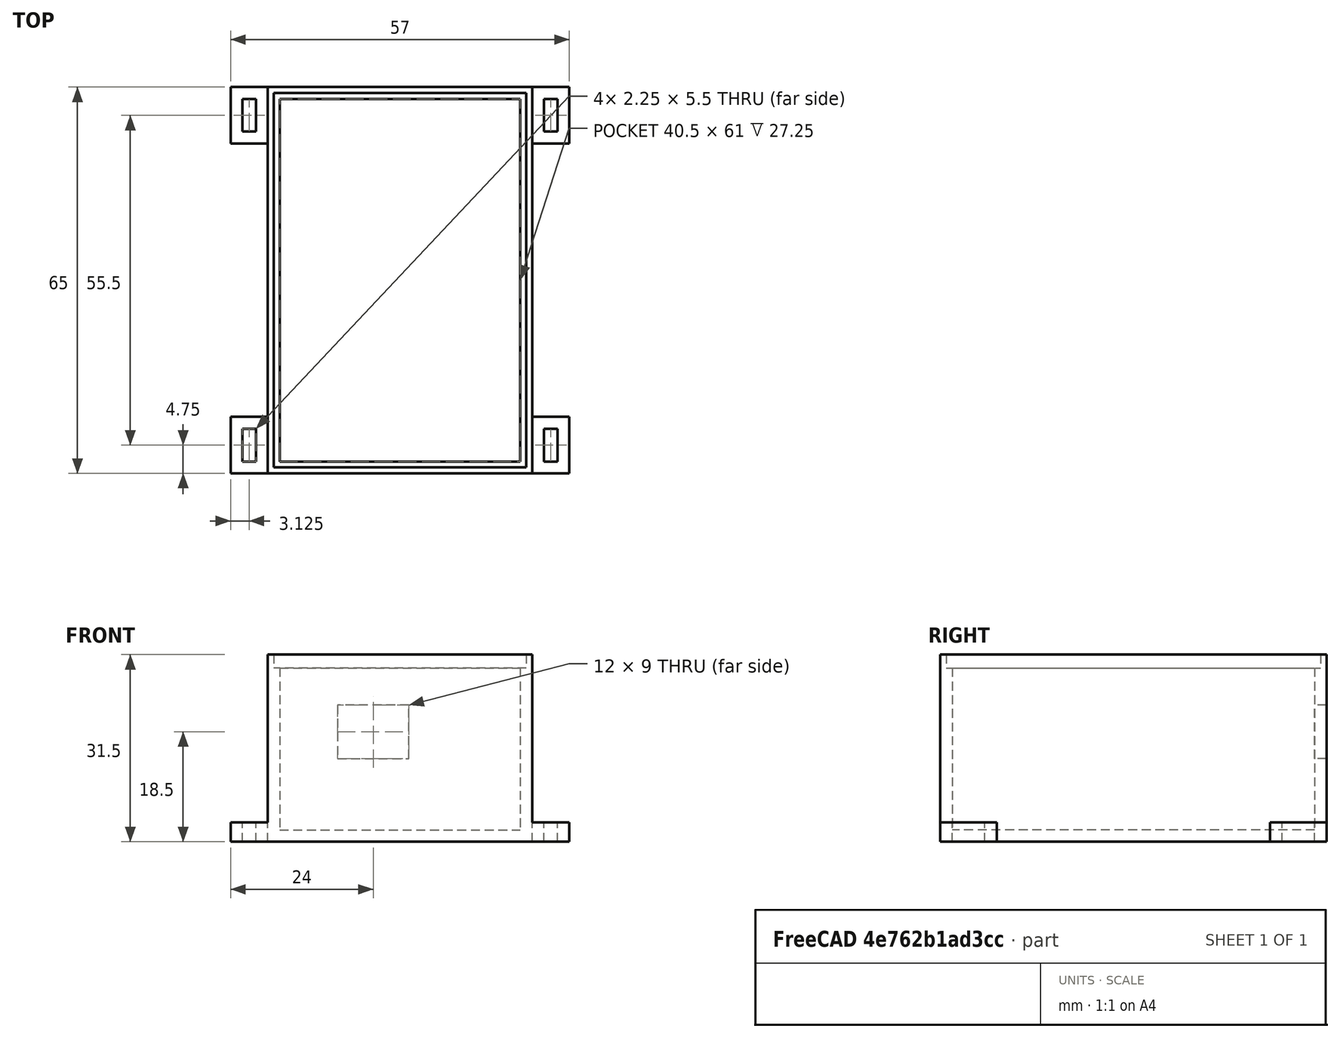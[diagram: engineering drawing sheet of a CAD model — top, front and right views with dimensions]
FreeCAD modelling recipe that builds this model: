
FCSTD DOCUMENT  (FreeCAD 0.19R)
Label: control-board-mount-base
License: All rights reserved
LicenseURL: http://en.wikipedia.org/wiki/All_rights_reserved
objects: Sketcher::SketchObject×5, PartDesign::Pocket×3, PartDesign::Pad×2, PartDesign::Body×1, Mesh::Feature×1
note: 16 computed .brp shape members not serialized (recipe doc carries the construction recipe); baked Part::Feature solids carry a one-line shape summary decoded from their .brp

FEATURE [Sketcher::SketchObject] Sketch
  FullyConstrained = true
  MapMode = 5
  Support = -> [XY_Plane]
  sketch-geometry (4):
    g0: LineSegment StartX=0 StartY=0 StartZ=0 EndX=44.5 EndY=0 EndZ=0
    g1: LineSegment StartX=44.5 StartY=0 StartZ=0 EndX=44.5 EndY=65 EndZ=0
    g2: LineSegment StartX=44.5 StartY=65 StartZ=0 EndX=0 EndY=65 EndZ=0
    g3: LineSegment StartX=0 StartY=65 StartZ=0 EndX=0 EndY=0 EndZ=0
  constraints (11):
    c: Coincident(g0,g1)
    c: Coincident(g1,g2)
    c: Coincident(g2,g3)
    c: Coincident(g3,g0)
    c: Horizontal(g0)
    c: Horizontal(g2)
    c: Vertical(g1)
    c: Vertical(g3)
    c: Coincident(g0,g-1)
    c: DistanceX(g2,g2) = 44.5
    c: DistanceY(g1,g1) = 65
FEATURE [PartDesign::Pad] Pad
  Direction = (1,1,1)
  Length = 31.5
  Length2 = 100
  Profile = -> Sketch
  Type = 0
FEATURE [Sketcher::SketchObject] Sketch001
  FullyConstrained = true
  MapMode = 5
  Placement = pos=(0,0,31.5) rot=(0,0,1;0rad)
  Support = -> [Pad]
  sketch-geometry (10):
    g0: LineSegment StartX=1 StartY=64 StartZ=0 EndX=43.5 EndY=64 EndZ=0
    g1: LineSegment StartX=43.5 StartY=64 StartZ=0 EndX=43.5 EndY=1 EndZ=0
    g2: LineSegment StartX=43.5 StartY=1 StartZ=0 EndX=1 EndY=1 EndZ=0
    g3: LineSegment StartX=1 StartY=1 StartZ=0 EndX=1 EndY=64 EndZ=0
    g4: LineSegment StartX=0 StartY=0 StartZ=0 EndX=44.5 EndY=0 EndZ=0
    g5: LineSegment StartX=44.5 StartY=0 StartZ=0 EndX=44.5 EndY=65 EndZ=0
    g6: LineSegment StartX=44.5 StartY=65 StartZ=0 EndX=0 EndY=65 EndZ=0
    g7: LineSegment StartX=0 StartY=65 StartZ=0 EndX=0 EndY=0 EndZ=0
    g8: LineSegment StartX=22.25 StartY=64 StartZ=0 EndX=22.25 EndY=65 EndZ=0
    g9: LineSegment StartX=43.5 StartY=32.5 StartZ=0 EndX=44.5 EndY=32.5 EndZ=0
  constraints (27):
    c: Coincident(g0,g1)
    c: Coincident(g1,g2)
    c: Coincident(g2,g3)
    c: Coincident(g3,g0)
    c: Horizontal(g0)
    c: Horizontal(g2)
    c: Vertical(g1)
    c: Vertical(g3)
    c: Coincident(g4,g5)
    c: Coincident(g5,g6)
    c: Coincident(g6,g7)
    c: Coincident(g7,g4)
    c: Horizontal(g4)
    c: Horizontal(g6)
    c: Vertical(g5)
    c: Vertical(g7)
    c: Coincident(g4,g-1)
    c: DistanceX(g6,g6) = 44.5
    c: DistanceY(g5,g5) = 65
    c: Vertical(g8)
    c: Horizontal(g9)
    c: Symmetric(g5,g6,g8)
    c: Symmetric(g0,g0,g8)
    c: Symmetric(g4,g5,g9)
    c: Symmetric(g1,g0,g9)
    c: DistanceX(g6,g0) = 1
    c: DistanceY(g0,g6) = 1
FEATURE [PartDesign::Pocket] Pocket
  BaseFeature = -> Pad
  Length = 2.25
  Length2 = 100
  Profile = -> Sketch001
  Type = 0
FEATURE [Sketcher::SketchObject] Sketch002
  FullyConstrained = true
  MapMode = 5
  Placement = pos=(0,0,29.25) rot=(0,0,1;0rad)
  Support = -> [Pocket]
  sketch-geometry (10):
    g0: LineSegment StartX=2 StartY=63 StartZ=0 EndX=42.5 EndY=63 EndZ=0
    g1: LineSegment StartX=42.5 StartY=63 StartZ=0 EndX=42.5 EndY=2 EndZ=0
    g2: LineSegment StartX=42.5 StartY=2 StartZ=0 EndX=2 EndY=2 EndZ=0
    g3: LineSegment StartX=2 StartY=2 StartZ=0 EndX=2 EndY=63 EndZ=0
    g4: LineSegment StartX=0 StartY=0 StartZ=0 EndX=44.5 EndY=0 EndZ=0
    g5: LineSegment StartX=44.5 StartY=0 StartZ=0 EndX=44.5 EndY=65 EndZ=0
    g6: LineSegment StartX=44.5 StartY=65 StartZ=0 EndX=0 EndY=65 EndZ=0
    g7: LineSegment StartX=0 StartY=65 StartZ=0 EndX=0 EndY=0 EndZ=0
    g8: LineSegment StartX=22.25 StartY=63 StartZ=0 EndX=22.25 EndY=65 EndZ=0
    g9: LineSegment StartX=42.5 StartY=32.5 StartZ=0 EndX=44.5 EndY=32.5 EndZ=0
  constraints (27):
    c: Coincident(g0,g1)
    c: Coincident(g1,g2)
    c: Coincident(g2,g3)
    c: Coincident(g3,g0)
    c: Horizontal(g0)
    c: Horizontal(g2)
    c: Vertical(g1)
    c: Vertical(g3)
    c: Coincident(g4,g5)
    c: Coincident(g5,g6)
    c: Coincident(g6,g7)
    c: Coincident(g7,g4)
    c: Horizontal(g4)
    c: Horizontal(g6)
    c: Vertical(g5)
    c: Vertical(g7)
    c: Coincident(g4,g-1)
    c: Vertical(g8)
    c: Horizontal(g9)
    c: Symmetric(g5,g6,g8)
    c: Symmetric(g0,g0,g8)
    c: Symmetric(g4,g5,g9)
    c: Symmetric(g1,g0,g9)
    c: DistanceX(g6,g6) = 44.5
    c: DistanceY(g5,g5) = 65
    c: DistanceX(g6,g0) = 2
    c: DistanceY(g0,g6) = 2
FEATURE [PartDesign::Pocket] Pocket001
  BaseFeature = -> Pocket
  Length = 27.25
  Length2 = 100
  Profile = -> Sketch002
  Type = 0
FEATURE [Sketcher::SketchObject] Sketch003
  FullyConstrained = true
  MapMode = 5
  Placement = pos=(0,65,0) rot=(0,0.707107,0.707107;3.14159rad)
  Support = -> [Pocket001]
  sketch-geometry (15):
    g0: LineSegment StartX=-23.75 StartY=23 StartZ=0 EndX=-11.75 EndY=23 EndZ=0
    g1: LineSegment StartX=-11.75 StartY=23 StartZ=0 EndX=-11.75 EndY=14 EndZ=0
    g2: LineSegment StartX=-11.75 StartY=14 StartZ=0 EndX=-23.75 EndY=14 EndZ=0
    g3: LineSegment StartX=-23.75 StartY=14 StartZ=0 EndX=-23.75 EndY=23 EndZ=0
    g4: LineSegment StartX=-2.25 StartY=2 StartZ=0 EndX=-42.25 EndY=2 EndZ=0
    g5: LineSegment StartX=-42.25 StartY=2 StartZ=0 EndX=-42.25 EndY=29 EndZ=0
    g6: LineSegment StartX=-42.25 StartY=29 StartZ=0 EndX=-2.25 EndY=29 EndZ=0
    g7: LineSegment StartX=-2.25 StartY=29 StartZ=0 EndX=-2.25 EndY=2 EndZ=0
    g8: GeomPoint X=-17.75 Y=14 Z=0
    g9: GeomPoint X=-11.75 Y=18.5 Z=0
    g10: LineSegment StartX=-44.5 StartY=31.5 StartZ=0 EndX=0 EndY=31.5 EndZ=0
    g11: LineSegment StartX=0 StartY=31.5 StartZ=0 EndX=0 EndY=0 EndZ=0
    g12: LineSegment StartX=0 StartY=0 StartZ=0 EndX=-44.5 EndY=0 EndZ=0
    g13: LineSegment StartX=-44.5 StartY=0 StartZ=0 EndX=-44.5 EndY=31.5 EndZ=0
    g14: LineSegment StartX=-22.25 StartY=29 StartZ=0 EndX=-22.25 EndY=31.5 EndZ=0
  constraints (39):
    c: Coincident(g0,g1)
    c: Coincident(g1,g2)
    c: Coincident(g2,g3)
    c: Coincident(g3,g0)
    c: Horizontal(g0)
    c: Horizontal(g2)
    c: Vertical(g1)
    c: Vertical(g3)
    c: Coincident(g4,g5)
    c: Coincident(g5,g6)
    c: Coincident(g6,g7)
    c: Coincident(g7,g4)
    c: Horizontal(g4)
    c: Horizontal(g6)
    c: Vertical(g5)
    c: Vertical(g7)
    c: DistanceX(g4,g4) = 40
    c: DistanceY(g7,g7) = 27
    c: DistanceX(g0,g0) = 12
    c: DistanceY(g3,g3) = 9
    c: Symmetric(g1,g0,g9)
    c: Symmetric(g1,g2,g8)
    c: DistanceX(g8,g4) = 15.5
    c: Coincident(g10,g11)
    c: Coincident(g11,g12)
    c: Coincident(g12,g13)
    c: Coincident(g13,g10)
    c: Horizontal(g10)
    c: Horizontal(g12)
    c: Vertical(g11)
    c: Vertical(g13)
    c: Coincident(g11,g-1)
    c: DistanceX(g10,g10) = 44.5
    c: Vertical(g14)
    c: Symmetric(g6,g5,g14)
    c: Symmetric(g10,g10,g14)
    c: DistanceY(g13,g13) = 31.5
    c: DistanceY(g12,g4) = 2
    c: DistanceY(g9,g6) = 10.5
FEATURE [PartDesign::Pocket] Pocket002
  BaseFeature = -> Pocket001
  Length = 5
  Length2 = 100
  Profile = -> Sketch003
  Type = 2
FEATURE [Sketcher::SketchObject] Sketch004
  FullyConstrained = true
  MapMode = 5
  Support = -> [XY_Plane]
  sketch-geometry (44):
    g0: LineSegment StartX=0 StartY=0 StartZ=0 EndX=44.5 EndY=0 EndZ=0
    g1: LineSegment StartX=44.5 StartY=0 StartZ=0 EndX=44.5 EndY=65 EndZ=0
    g2: LineSegment StartX=44.5 StartY=65 StartZ=0 EndX=0 EndY=65 EndZ=0
    g3: LineSegment StartX=0 StartY=65 StartZ=0 EndX=0 EndY=0 EndZ=0
    g4: LineSegment StartX=44.5 StartY=65 StartZ=0 EndX=50.75 EndY=65 EndZ=0
    g5: LineSegment StartX=50.75 StartY=65 StartZ=0 EndX=50.75 EndY=55.5 EndZ=0
    g6: LineSegment StartX=50.75 StartY=55.5 StartZ=0 EndX=44.5 EndY=55.5 EndZ=0
    g7: LineSegment StartX=44.5 StartY=55.5 StartZ=0 EndX=44.5 EndY=65 EndZ=0
    g8: LineSegment StartX=44.5 StartY=0 StartZ=0 EndX=50.75 EndY=0 EndZ=0
    g9: LineSegment StartX=50.75 StartY=0 StartZ=0 EndX=50.75 EndY=9.5 EndZ=0
    g10: LineSegment StartX=50.75 StartY=9.5 StartZ=0 EndX=44.5 EndY=9.5 EndZ=0
    g11: LineSegment StartX=44.5 StartY=9.5 StartZ=0 EndX=44.5 EndY=0 EndZ=0
    g12: LineSegment StartX=0 StartY=0 StartZ=0 EndX=-6.25 EndY=0 EndZ=0
    g13: LineSegment StartX=-6.25 StartY=0 StartZ=0 EndX=-6.25 EndY=9.5 EndZ=0
    g14: LineSegment StartX=-6.25 StartY=9.5 StartZ=0 EndX=0 EndY=9.5 EndZ=0
    g15: LineSegment StartX=0 StartY=9.5 StartZ=0 EndX=0 EndY=0 EndZ=0
    g16: LineSegment StartX=0 StartY=65 StartZ=0 EndX=-6.25 EndY=65 EndZ=0
    g17: LineSegment StartX=-6.25 StartY=65 StartZ=0 EndX=-6.25 EndY=55.5 EndZ=0
    g18: LineSegment StartX=-6.25 StartY=55.5 StartZ=0 EndX=0 EndY=55.5 EndZ=0
    g19: LineSegment StartX=0 StartY=55.5 StartZ=0 EndX=0 EndY=65 EndZ=0
    g20: LineSegment StartX=46.5 StartY=63 StartZ=0 EndX=48.75 EndY=63 EndZ=0
    g21: LineSegment StartX=48.75 StartY=63 StartZ=0 EndX=48.75 EndY=57.5 EndZ=0
    g22: LineSegment StartX=48.75 StartY=57.5 StartZ=0 EndX=46.5 EndY=57.5 EndZ=0
    g23: LineSegment StartX=46.5 StartY=57.5 StartZ=0 EndX=46.5 EndY=63 EndZ=0
    g24: LineSegment StartX=46.5 StartY=7.5 StartZ=0 EndX=48.75 EndY=7.5 EndZ=0
    g25: LineSegment StartX=48.75 StartY=7.5 StartZ=0 EndX=48.75 EndY=2 EndZ=0
    g26: LineSegment StartX=48.75 StartY=2 StartZ=0 EndX=46.5 EndY=2 EndZ=0
    g27: LineSegment StartX=46.5 StartY=2 StartZ=0 EndX=46.5 EndY=7.5 EndZ=0
    g28: LineSegment StartX=-4.25 StartY=7.5 StartZ=0 EndX=-2 EndY=7.5 EndZ=0
    g29: LineSegment StartX=-2 StartY=7.5 StartZ=0 EndX=-2 EndY=2 EndZ=0
    g30: LineSegment StartX=-2 StartY=2 StartZ=0 EndX=-4.25 EndY=2 EndZ=0
    g31: LineSegment StartX=-4.25 StartY=2 StartZ=0 EndX=-4.25 EndY=7.5 EndZ=0
    g32: LineSegment StartX=-4.25 StartY=63 StartZ=0 EndX=-2 EndY=63 EndZ=0
    g33: LineSegment StartX=-2 StartY=63 StartZ=0 EndX=-2 EndY=57.5 EndZ=0
    g34: LineSegment StartX=-2 StartY=57.5 StartZ=0 EndX=-4.25 EndY=57.5 EndZ=0
    g35: LineSegment StartX=-4.25 StartY=57.5 StartZ=0 EndX=-4.25 EndY=63 EndZ=0
    g36: LineSegment StartX=-3.125 StartY=63 StartZ=0 EndX=-3.125 EndY=65 EndZ=0
    g37: LineSegment StartX=-4.25 StartY=60.25 StartZ=0 EndX=-6.25 EndY=60.25 EndZ=0
    g38: LineSegment StartX=47.625 StartY=63 StartZ=0 EndX=47.625 EndY=65 EndZ=0
    g39: LineSegment StartX=48.75 StartY=60.25 StartZ=0 EndX=50.75 EndY=60.25 EndZ=0
    g40: LineSegment StartX=-3.125 StartY=7.5 StartZ=0 EndX=-3.125 EndY=9.5 EndZ=0
    g41: LineSegment StartX=-4.25 StartY=4.75 StartZ=0 EndX=-6.25 EndY=4.75 EndZ=0
    g42: LineSegment StartX=47.625 StartY=7.5 StartZ=0 EndX=47.625 EndY=9.5 EndZ=0
    g43: LineSegment StartX=48.75 StartY=4.75 StartZ=0 EndX=50.75 EndY=4.75 EndZ=0
  constraints (119):
    c: Coincident(g0,g1)
    c: Coincident(g1,g2)
    c: Coincident(g2,g3)
    c: Coincident(g3,g0)
    c: Horizontal(g0)
    c: Horizontal(g2)
    c: Vertical(g1)
    c: Vertical(g3)
    c: Coincident(g0,g-1)
    c: Coincident(g4,g5)
    c: Coincident(g5,g6)
    c: Coincident(g6,g7)
    c: Coincident(g7,g4)
    c: Horizontal(g4)
    c: Horizontal(g6)
    c: Vertical(g5)
    c: Vertical(g7)
    c: Coincident(g4,g1)
    c: Coincident(g8,g9)
    c: Coincident(g9,g10)
    c: Coincident(g10,g11)
    c: Coincident(g11,g8)
    c: Horizontal(g8)
    c: Horizontal(g10)
    c: Vertical(g9)
    c: Vertical(g11)
    c: Coincident(g8,g0)
    c: Coincident(g12,g13)
    c: Coincident(g13,g14)
    c: Coincident(g14,g15)
    c: Coincident(g15,g12)
    c: Horizontal(g12)
    c: Horizontal(g14)
    c: Vertical(g13)
    c: Vertical(g15)
    c: Coincident(g12,g-1)
    c: Coincident(g16,g17)
    c: Coincident(g17,g18)
    c: Coincident(g18,g19)
    c: Coincident(g19,g16)
    c: Horizontal(g16)
    c: Horizontal(g18)
    c: Vertical(g17)
    c: Vertical(g19)
    c: Coincident(g16,g2)
    c: Coincident(g20,g21)
    c: Coincident(g21,g22)
    c: Coincident(g22,g23)
    c: Coincident(g23,g20)
    c: Horizontal(g20)
    c: Horizontal(g22)
    c: Vertical(g21)
    c: Vertical(g23)
    c: Coincident(g24,g25)
    c: Coincident(g25,g26)
    c: Coincident(g26,g27)
    c: Coincident(g27,g24)
    c: Horizontal(g24)
    c: Horizontal(g26)
    c: Vertical(g25)
    c: Vertical(g27)
    c: Coincident(g28,g29)
    c: Coincident(g29,g30)
    c: Coincident(g30,g31)
    c: Coincident(g31,g28)
    c: Horizontal(g28)
    c: Horizontal(g30)
    c: Vertical(g29)
    c: Vertical(g31)
    c: Coincident(g32,g33)
    c: Coincident(g33,g34)
    c: Coincident(g34,g35)
    c: Coincident(g35,g32)
    c: Horizontal(g32)
    c: Horizontal(g34)
    c: Vertical(g33)
    c: Vertical(g35)
    c: DistanceX(g2,g2) = 44.5
    c: DistanceY(g1,g1) = 65
    c: Equal(g32,g20)
    c: Equal(g20,g24)
    c: Equal(g24,g28)
    c: Equal(g33,g21)
    c: Equal(g21,g25)
    c: Equal(g25,g29)
    c: Equal(g16,g4)
    c: Equal(g4,g10)
    c: Equal(g10,g14)
    c: Equal(g17,g5)
    c: Equal(g5,g9)
    c: Equal(g9,g13)
    c: Vertical(g36)
    c: Horizontal(g37)
    c: DistanceY(g33,g33) = 5.5
    c: DistanceX(g16,g32) = 2
    c: DistanceY(g32,g16) = 2
    c: Symmetric(g32,g32,g36)
    c: Symmetric(g16,g16,g36)
    c: Symmetric(g34,g32,g37)
    c: Symmetric(g17,g16,g37)
    c: DistanceX(g34,g34) = 2.25
    c: Vertical(g38)
    c: Horizontal(g39)
    c: Symmetric(g20,g20,g38)
    c: Symmetric(g20,g21,g39)
    c: Symmetric(g4,g4,g38)
    c: Symmetric(g4,g5,g39)
    c: Vertical(g40)
    c: Horizontal(g41)
    c: Symmetric(g28,g28,g40)
    c: Symmetric(g30,g28,g41)
    c: Symmetric(g14,g13,g40)
    c: Symmetric(g12,g13,g41)
    c: Vertical(g42)
    c: Horizontal(g43)
    c: Symmetric(g9,g10,g42)
    c: Symmetric(g24,g24,g42)
    c: Symmetric(g25,g24,g43)
    c: Symmetric(g8,g9,g43)
FEATURE [PartDesign::Pad] Pad001
  BaseFeature = -> Pocket002
  Direction = (1,1,1)
  Length = 3.25
  Length2 = 100
  Profile = -> Sketch004
  Type = 0
FEATURE [PartDesign::Body] Body
  Group = -> [Sketch,Pad,Sketch001,Pocket,Sketch002,Pocket001,Sketch003,Pocket002,Sketch004,Pad001]
  Origin = -> Origin
  Tip = -> Pad001
FEATURE [Mesh::Feature] Mesh  label="Body (Meshed)"
